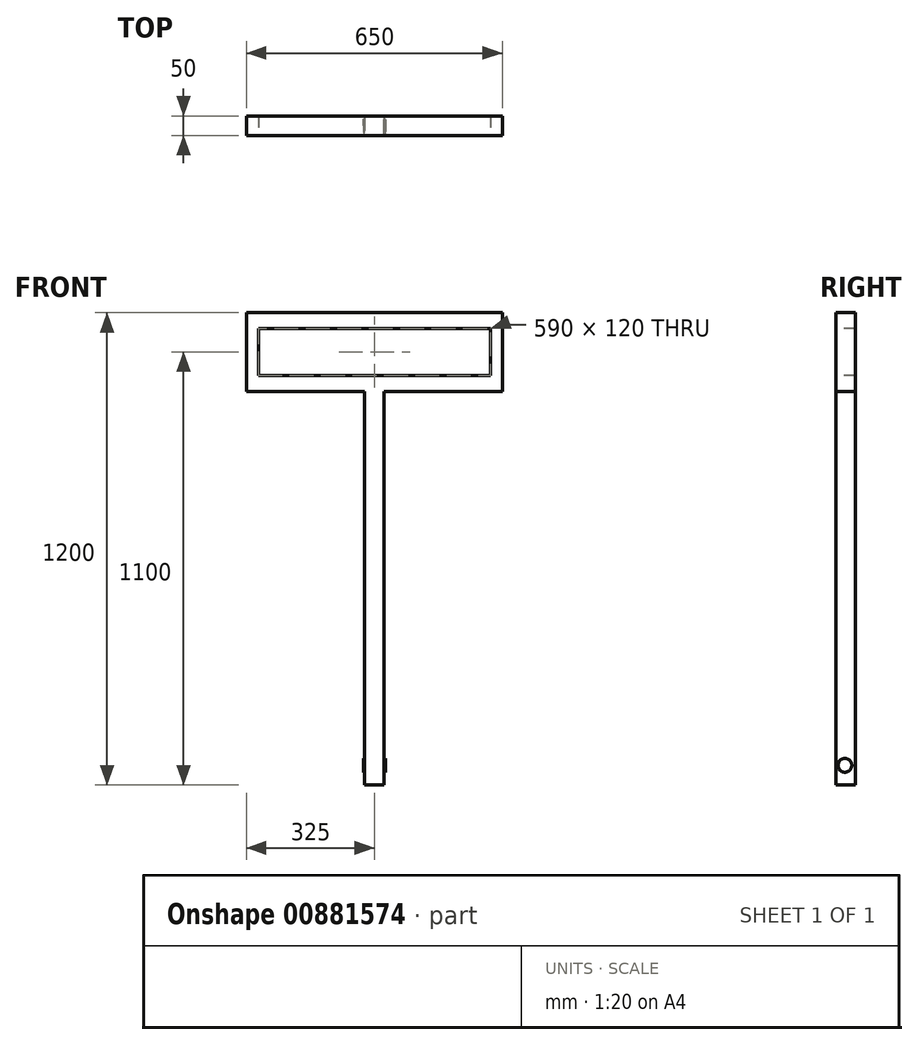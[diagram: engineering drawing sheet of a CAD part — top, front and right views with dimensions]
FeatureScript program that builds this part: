
annotation { "Feature Type Name" : "Feature", "Feature Type Description" : "" }
export const myFeature = defineFeature(function(context is Context, id is Id, definition is map)
    precondition{}
    {
        {
            var Q0;
            Q0=qCreatedBy(makeId("Top.planeOp"),FACE);
            var sketch = newSketch(context, id + "F0", { "sketchPlane" : qUnion([Q0])});
            skLineSegment(sketch, "E0.bottom", {"start": v(-25, 27.42) * mm, "end": v(25, 27.42) * mm});
            skLineSegment(sketch, "E0.top", {"start": v(-25, -22.58) * mm, "end": v(25, -22.58) * mm});
            skLineSegment(sketch, "E0.left", {"start": v(-25, 27.42) * mm, "end": v(-25, -22.58) * mm});
            skLineSegment(sketch, "E0.right", {"start": v(25, 27.42) * mm, "end": v(25, -22.58) * mm});
            skPoint(sketch, "E0.middle", {"position": v(0, 2.42) * mm});
            skSolve(sketch);
        }
        {
            var Q0;
            Q0=makeQuery(id+"F0.imprint","IMPRINT",FACE,{"disambiguationData":[TD([[makeQuery(id+"F0.imprint","IMPRINT",EDGE,{"derivedFrom":sQuery(id+"F0.wireOp",EDGE,"E0.bottom")}),-1.0]])]});
            extrude(context, id + "F1", {"entities" : qUnion([Q0]), "depth" : 1000 * mm, "offsetDistance" : 25 * mm});
        }
        {
            var Q0;
            Q0=makeQuery(id+"F1.opExtrude","SWEPT_FACE",FACE,{"disambiguationData":[OSD([sQuery(id+"F0.wireOp",EDGE,"E0.top")])]});
            var sketch = newSketch(context, id + "F2", { "sketchPlane" : qUnion([Q0])});
            skLineSegment(sketch, "E1", {"start": v(25, 1000) * mm, "end": v(325, 1000) * mm});
            skLineSegment(sketch, "E2", {"start": v(325, 1000) * mm, "end": v(325, 1200) * mm});
            skLineSegment(sketch, "E3", {"start": v(325, 1200) * mm, "end": v(-325, 1200) * mm});
            skLineSegment(sketch, "E4", {"start": v(-325, 1200) * mm, "end": v(-325, 1000) * mm});
            skLineSegment(sketch, "E5", {"start": v(-325, 1000) * mm, "end": v(25, 1000) * mm});
            skLineSegment(sketch, "E6.0", {"start": v(-295, 1040) * mm, "end": v(25, 1040) * mm});
            skLineSegment(sketch, "E7.0", {"start": v(25, 1040) * mm, "end": v(295, 1040) * mm});
            skLineSegment(sketch, "E8.0", {"start": v(-295, 1160) * mm, "end": v(-295, 1040) * mm});
            skLineSegment(sketch, "E9.0", {"start": v(295, 1040) * mm, "end": v(295, 1160) * mm});
            skLineSegment(sketch, "E10.0", {"start": v(295, 1160) * mm, "end": v(-295, 1160) * mm});
            skSolve(sketch);
        }
        {
            var Q0;
            {var subQ3=sQuery(id+"F2.wireOp",EDGE,"E1");Q0=makeQuery(id+"F2.imprint","IMPRINT",FACE,{"disambiguationData":[TD([[makeQuery(id+"F2.imprint","IMPRINT",EDGE,{"derivedFrom":subQ3}),1.0]])]});}
            extrude(context, id + "F3", {"entities" : qUnion([Q0]), "operationType" : NewBodyOperationType.ADD, "oppositeDirection" : true, "depth" : 50 * mm, "offsetDistance" : 25 * mm});
        }
        {
            var Q0;
            Q0=makeQuery(id+"F1.opExtrude","SWEPT_FACE",FACE,{"disambiguationData":[OSD([sQuery(id+"F0.wireOp",EDGE,"E0.right")])]});
            var sketch = newSketch(context, id + "F4", { "sketchPlane" : qUnion([Q0])});
            skCircle(sketch, "E11", {"center": v(0, 50) * mm, "radius": 17.5 * mm});
            skSolve(sketch);
        }
        {
            var Q0;
            Q0 = qSketchRegion(id + "F4", true);
            extrude(context, id + "F5", {"entities" : qUnion([Q0]), "operationType" : NewBodyOperationType.ADD, "depth" : 3 * mm, "offsetDistance" : 25 * mm});
        }
        {
            var Q0;
            Q0=makeQuery(id+"F1.opExtrude","SWEPT_FACE",FACE,{"disambiguationData":[OSD([sQuery(id+"F0.wireOp",EDGE,"E0.left")])]});
            var sketch = newSketch(context, id + "F6", { "sketchPlane" : qUnion([Q0])});
            skLineSegment(sketch, "E12", {"start": v(22.58, 0) * mm, "end": v(22.58, 50) * mm});
            skLineSegment(sketch, "E13", {"start": v(22.58, 50) * mm, "end": v(-2.42, 50) * mm});
            skCircle(sketch, "E14", {"center": v(-2.42, 50) * mm, "radius": 17.5 * mm});
            skSolve(sketch);
        }
        {
            var Q0;
            Q0 = qSketchRegion(id + "F6", true);
            extrude(context, id + "F7", {"entities" : qUnion([Q0]), "operationType" : NewBodyOperationType.ADD, "depth" : 3 * mm, "offsetDistance" : 25 * mm});
        }
    });
